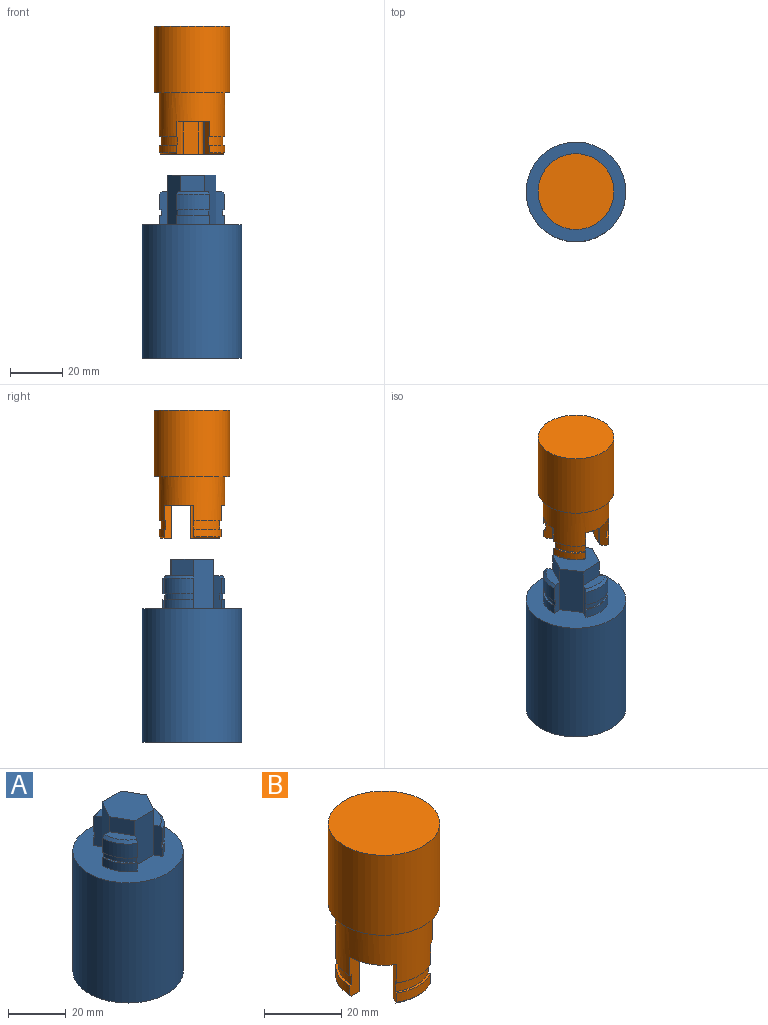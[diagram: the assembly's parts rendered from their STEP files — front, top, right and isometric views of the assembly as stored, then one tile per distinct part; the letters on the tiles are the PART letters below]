
ASSEMBLY  parts=2 mates=2
PART A: 37 faces, bbox 38.1x38.1x69.9 mm
  f0: plane 11.46x3.51mm, normal (0,0,1), area 32.2mm2, adj f2,f3,f32,f33
  f1: plane 9.92x6.87mm, normal (0,0,1), area 32.2mm2, adj f5,f7,f24,f35
  f2: plane 12.7x2.85mm, normal (-0.87,-0.5,0), area 39.8mm2, adj f0,f10,f14,f17,f20,f29,f30,f31
  f3: plane 12.7x2.85mm, normal (0.87,-0.5,0), area 39.8mm2, adj f0,f10,f15,f17,f20,f29,f30,f31
  f4: plane 12.7x2.85mm, normal (0.87,-0.5,0), area 39.8mm2, adj f9,f11,f16,f17,f19,f25,f26,f27
  f5: plane 12.7x2.85mm, normal (-0.87,-0.5,0), area 39.8mm2, adj f1,f8,f16,f17,f18,f21,f22,f23
  f6: plane 12.7x3.29mm, normal (0,1,0), area 39.8mm2, adj f9,f11,f14,f17,f19,f25,f26,f27
  f7: plane 12.7x3.29mm, normal (0,1,0), area 39.8mm2, adj f1,f8,f15,f17,f18,f21,f22,f23
  f8: cylinder r=12.47mm len=10.8mm, axis (0,0,1), area 77.6mm2, adj f5,f7,f23,f24
  f9: cylinder r=12.47mm len=10.8mm, axis (0,0,1), area 77.6mm2, adj f4,f6,f27,f28
  f10: cylinder r=12.47mm len=12.47mm, axis (0,0,1), area 77.6mm2, adj f2,f3,f30,f32
  f11: plane 9.92x6.87mm, normal (0,0,1), area 32.2mm2, adj f4,f6,f28,f34
  f12: cylinder r=19.05mm len=50.8mm, axis (0,0,1), area 6080.5mm2, adj f13,f17
  f13: plane 38.1x38.1mm, normal (0,0,-1), area 1140.1mm2, adj f12
  f14: plane 19.05x7.95mm, normal (-0.87,0.5,0), area 174.9mm2, adj f2,f6,f17,f33,f34,f36
  f15: plane 19.05x7.95mm, normal (0.87,0.5,0), area 174.9mm2, adj f3,f7,f17,f33,f35,f36
  f16: plane 19.05x9.18mm, normal (0,-1,0), area 174.9mm2, adj f4,f5,f17,f34,f35,f36
  f17: plane 38.1x38.1mm, normal (0,0,1), area 786.3mm2, adj f2,f3,f4,f5,f6,f7,f12,f14
  f18: cylinder r=12.47mm len=10.8mm, axis (0,0,1), area 46.4mm2, adj f5,f7,f17,f21
  f19: cylinder r=12.47mm len=10.8mm, axis (0,0,1), area 46.4mm2, adj f4,f6,f17,f25
  f20: cylinder r=12.47mm len=12.47mm, axis (0,0,1), area 46.4mm2, adj f2,f3,f17,f31
  f21: plane 10.8x6.57mm, normal (0,0,1), area 8.4mm2, adj f5,f7,f18,f22
  f22: cylinder r=11.81mm len=10.23mm, axis (0,0,1), area 27mm2, adj f5,f7,f21,f23
  f23: plane 10.8x6.57mm, normal (0,0,-1), area 8.4mm2, adj f5,f7,f8,f22
  f24: cone r=11.46mm half-angle=45deg, axis (0,0,-1), area 18mm2, adj f1,f5,f7,f8
  f25: plane 10.8x6.57mm, normal (0,0,1), area 8.4mm2, adj f4,f6,f19,f26
  f26: cylinder r=11.81mm len=10.23mm, axis (0,0,1), area 27mm2, adj f4,f6,f25,f27
  f27: plane 10.8x6.57mm, normal (0,0,-1), area 8.4mm2, adj f4,f6,f9,f26
  f28: cone r=11.46mm half-angle=45deg, axis (0,0,-1), area 18mm2, adj f4,f6,f9,f11
  f29: cylinder r=11.81mm len=11.81mm, axis (0,0,1), area 27mm2, adj f2,f3,f30,f31
  f30: plane 12.47x2.24mm, normal (0,0,-1), area 8.4mm2, adj f2,f3,f10,f29
  f31: plane 12.47x2.24mm, normal (0,0,1), area 8.4mm2, adj f2,f3,f20,f29
  f32: cone r=11.46mm half-angle=45deg, axis (0,0,-1), area 18mm2, adj f0,f2,f3,f10
  f33: plane 9.18x6.35mm, normal (0,1,0), area 58.3mm2, adj f0,f14,f15,f36
  f34: plane 7.95x6.35mm, normal (-0.87,-0.5,0), area 58.3mm2, adj f11,f14,f16,f36
  f35: plane 7.95x6.35mm, normal (0.87,-0.5,0), area 58.3mm2, adj f1,f15,f16,f36
  f36: plane 18.36x15.9mm, normal (0,0,1), area 219mm2, adj f14,f15,f16,f33,f34,f35
PART B: 44 faces, bbox 28.9x28.9x49 mm
  f0: plane 10.29x7.29mm, normal (0,0,-1), area 36.9mm2, adj f7,f9,f19,f23,f24,f43
  f1: plane 11.88x3.93mm, normal (0,0,-1), area 36.9mm2, adj f6,f10,f21,f26,f27,f39
  f2: plane 10.29x7.29mm, normal (0,0,-1), area 36.9mm2, adj f8,f11,f20,f29,f30,f35
  f3: cylinder r=12.51mm len=10.83mm, axis (0,0,1), area 38.2mm2, adj f8,f11,f34,f35
  f4: cylinder r=12.51mm len=10.83mm, axis (0,0,1), area 38.2mm2, adj f7,f9,f40,f43
  f5: cylinder r=12.51mm len=12.51mm, axis (0,0,1), area 38.2mm2, adj f6,f10,f38,f39
  f6: plane 12.7x2.88mm, normal (0.87,0.5,0), area 39.9mm2, adj f1,f5,f12,f16,f26,f36,f37,f38
  f7: plane 12.7x3.33mm, normal (0,-1,0), area 39.9mm2, adj f0,f4,f12,f16,f19,f40,f41,f42
  f8: plane 12.7x2.88mm, normal (0.87,0.5,0), area 39.9mm2, adj f2,f3,f12,f17,f20,f32,f33,f34
  f9: plane 12.7x2.88mm, normal (-0.87,0.5,0), area 39.9mm2, adj f0,f4,f12,f17,f23,f40,f41,f42
  f10: plane 12.7x2.88mm, normal (-0.87,0.5,0), area 39.9mm2, adj f1,f5,f12,f18,f21,f36,f37,f38
  f11: plane 12.7x3.33mm, normal (0,-1,0), area 39.9mm2, adj f2,f3,f12,f18,f29,f32,f33,f34
  f12: cylinder r=12.51mm len=25.02mm, axis (0,0,1), area 1093mm2, adj f6,f7,f8,f9,f10,f11,f15,f16
  f13: cylinder r=14.47mm len=28.93mm, axis (0,0,-1), area 2308.6mm2, adj f14,f15
  f14: plane 28.93x28.93mm, normal (0,0,1), area 657.4mm2, adj f13
  f15: plane 28.93x28.93mm, normal (0,0,-1), area 165.7mm2, adj f12,f13
  f16: plane 10.83x7.92mm, normal (0,0,-1), area 45mm2, adj f6,f7,f12,f19,f25,f26
  f17: plane 12.51x4.56mm, normal (0,0,-1), area 45mm2, adj f8,f9,f12,f20,f22,f23
  f18: plane 10.83x7.92mm, normal (0,0,-1), area 45mm2, adj f10,f11,f12,f21,f28,f29
  f19: cylinder r=1.59mm len=19.05mm, axis (0,0,-1), area 42.2mm2, adj f0,f7,f16,f24,f25,f31
  f20: cylinder r=1.59mm len=19.05mm, axis (0,0,-1), area 42.2mm2, adj f2,f8,f17,f22,f30,f31
  f21: cylinder r=1.59mm len=19.05mm, axis (0,0,-1), area 42.2mm2, adj f1,f10,f18,f27,f28,f31
  f22: plane 6.35x6.01mm, normal (0,-1,0), area 38.1mm2, adj f17,f20,f23,f31
  f23: cylinder r=1.59mm len=19.05mm, axis (0,0,-1), area 42.2mm2, adj f0,f9,f17,f22,f24,f31
  f24: plane 19.05x5.2mm, normal (-0.87,-0.5,0), area 114.4mm2, adj f0,f19,f23,f31
  f25: plane 6.35x5.2mm, normal (-0.87,0.5,0), area 38.1mm2, adj f16,f19,f26,f31
  f26: cylinder r=1.59mm len=19.05mm, axis (0,0,-1), area 42.2mm2, adj f1,f6,f16,f25,f27,f31
  f27: plane 19.05x6.01mm, normal (0,1,0), area 114.4mm2, adj f1,f21,f26,f31
  f28: plane 6.35x5.2mm, normal (0.87,0.5,0), area 38.1mm2, adj f18,f21,f29,f31
  f29: cylinder r=1.59mm len=19.05mm, axis (0,0,-1), area 42.2mm2, adj f2,f11,f18,f28,f30,f31
  f30: plane 19.05x5.2mm, normal (0.87,-0.5,0), area 114.4mm2, adj f2,f20,f29,f31
  f31: plane 18.36x16.33mm, normal (0,0,-1), area 221.7mm2, adj f19,f20,f21,f22,f23,f24,f25,f26
  f32: cylinder r=11.81mm len=10.23mm, axis (0,0,-1), area 39.3mm2, adj f8,f11,f33,f34
  f33: plane 10.83x6.6mm, normal (0,0,-1), area 8.9mm2, adj f8,f11,f12,f32
  f34: plane 10.83x6.6mm, normal (0,0,1), area 8.9mm2, adj f3,f8,f11,f32
  f35: cone r=12.51mm half-angle=44.5deg, axis (0,0,1), area 11.5mm2, adj f2,f3,f8,f11
  f36: cylinder r=11.81mm len=11.81mm, axis (0,0,-1), area 39.3mm2, adj f6,f10,f37,f38
  f37: plane 12.51x2.28mm, normal (0,0,-1), area 8.9mm2, adj f6,f10,f12,f36
  f38: plane 12.51x2.28mm, normal (0,0,1), area 8.9mm2, adj f5,f6,f10,f36
  f39: cone r=12.51mm half-angle=44.5deg, axis (0,0,1), area 11.5mm2, adj f1,f5,f6,f10
  f40: plane 10.83x6.6mm, normal (0,0,1), area 8.9mm2, adj f4,f7,f9,f42
  f41: plane 10.83x6.6mm, normal (0,0,-1), area 8.9mm2, adj f7,f9,f12,f42
  f42: cylinder r=11.81mm len=10.23mm, axis (0,0,-1), area 39.3mm2, adj f7,f9,f40,f41
  f43: cone r=12.51mm half-angle=44.5deg, axis (0,0,1), area 11.5mm2, adj f0,f4,f7,f9
PLACE A rot(axis=(0,0,-1),57.3deg) t=(-3.4,25.64,-143.6)mm
PLACE B rot(axis=(0,0,-1),57.3deg) t=(-3.4,25.64,-105.75)mm
MATE cylindrical B.f32 <-> A.f12  axis (0,0,-1) through (-3.4,25.64,-110.33)mm
MATE parallel B.f10 <-> A.f4  axis (-0.05,1,0) through (-14.15,25.13,-122.93)mm
